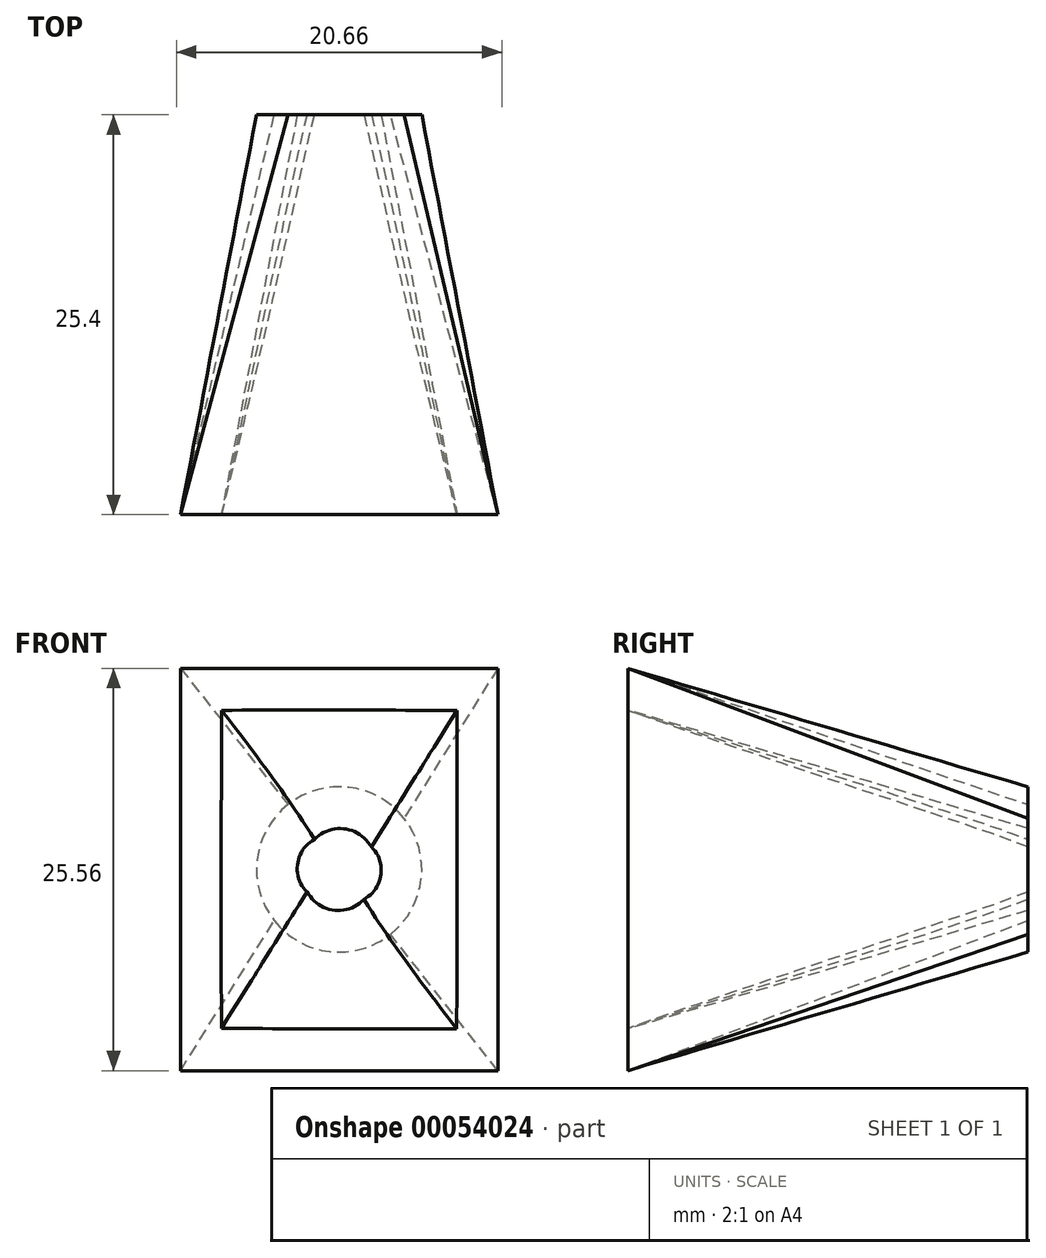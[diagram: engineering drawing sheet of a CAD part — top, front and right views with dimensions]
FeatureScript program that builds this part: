
annotation { "Feature Type Name" : "Feature", "Feature Type Description" : "" }
export const myFeature = defineFeature(function(context is Context, id is Id, definition is map)
    precondition{}
    {
        {
            var Q0;
            Q0=qCreatedBy(makeId("Front.planeOp"),FACE);
            var sketch = newSketch(context, id + "F0", { "sketchPlane" : qUnion([Q0])});
            skCircle(sketch, "E0", {"center": v(0, 0) * mm, "radius": 5.25 * mm});
            skSolve(sketch);
        }
        {
            var Q0;
            Q0=qCreatedBy(makeId("Front.planeOp"),FACE);
            cPlane(context, id + "F1", {"entities" : qUnion([Q0]), "cplaneType" : CPlaneType.OFFSET, "offset" : 25.4 * mm, "width" : 152.4 * mm, "height" : 152.4 * mm});
        }
        {
            var Q0;
            Q0=qCreatedBy(id+"F1.planeOp",FACE);
            var sketch = newSketch(context, id + "F2", { "sketchPlane" : qUnion([Q0])});
            skLineSegment(sketch, "E1.rect.bottom", {"start": v(-10.08, 12.78) * mm, "end": v(10.08, 12.78) * mm});
            skLineSegment(sketch, "E1.rect.top", {"start": v(-10.08, -12.78) * mm, "end": v(10.08, -12.78) * mm});
            skLineSegment(sketch, "E1.rect.left", {"start": v(-10.08, 12.78) * mm, "end": v(-10.08, -12.78) * mm});
            skLineSegment(sketch, "E1.rect.right", {"start": v(10.08, 12.78) * mm, "end": v(10.08, -12.78) * mm});
            skPoint(sketch, "E1.rect.middle", {"position": v(0, 0) * mm});
            skSolve(sketch);
        }
        {
            var Q0;
            Q0=makeQuery(id+"F2.imprint","IMPRINT",FACE,{"disambiguationData":[TD([[makeQuery(id+"F2.imprint","IMPRINT",EDGE,{"derivedFrom":sQuery(id+"F2.wireOp",EDGE,"E1.rect.bottom")}),-1.0]])]});
            var Q1;
            Q1=makeQuery(id+"F0.imprint","IMPRINT",FACE,{"disambiguationData":[TD([[makeQuery(id+"F0.imprint","IMPRINT",EDGE,{"derivedFrom":sQuery(id+"F0.wireOp",EDGE,"E0")}),1.0]])]});
            var Q2;
            Q2=qCreatedBy(makeId("Origin.pointOp"),VERTEX);
            var Q3;
            Q3=sQuery(id+"F0.wireOp",VERTEX,"E0.center");
            var Q4;
            Q4=sQuery(id+"F2.wireOp",VERTEX,"E1.rect.middle");
            loft(context, id + "F3", {"sheetProfilesArray" : [{ "sheetProfileEntities" : qUnion([Q0]) }, { "sheetProfileEntities" : qUnion([Q1]) }], "connections" : [{ "connectionEntities" : qUnion([Q2, Q3, Q4]), "connectionEdgeQueries" : qUnion([]), "connectionEdgeParameters" : [] }]});
        }
        {
            var Q0;
            Q0=makeQuery(id+"F3.opLoft","CAP_FACE",FACE,{"disambiguationData":[OSD([makeQuery(id+"F0.imprint","IMPRINT",FACE,{"disambiguationData":[TD([[makeQuery(id+"F0.imprint","IMPRINT",EDGE,{"derivedFrom":sQuery(id+"F0.wireOp",EDGE,"E0")}),1.0]])]})])],"isStart":true});
            var Q1;
            Q1=makeQuery(id+"F3.opLoft","CAP_FACE",FACE,{"disambiguationData":[OSD([makeQuery(id+"F2.imprint","IMPRINT",FACE,{"disambiguationData":[TD([[makeQuery(id+"F2.imprint","IMPRINT",EDGE,{"derivedFrom":sQuery(id+"F2.wireOp",EDGE,"E1.rect.bottom")}),-1.0]])]})])],"isStart":true});
            shell(context, id + "F4", {"entities" : qUnion([Q0, Q1]), "thickness" : 2.54 * mm});
        }
    });
